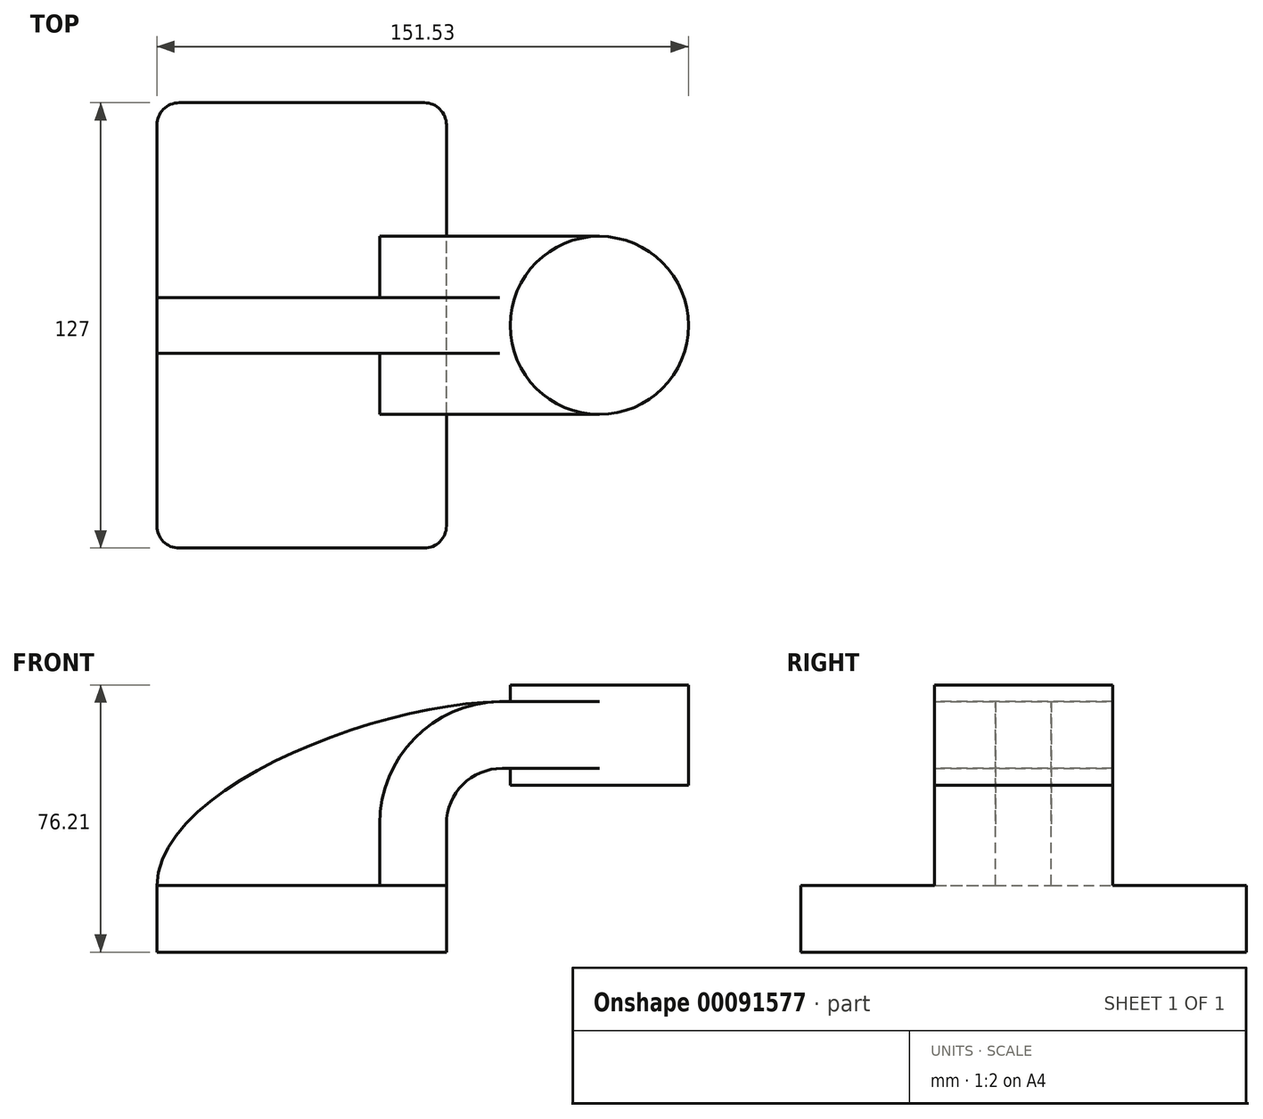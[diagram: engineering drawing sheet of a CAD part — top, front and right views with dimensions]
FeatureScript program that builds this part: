
annotation { "Feature Type Name" : "Feature", "Feature Type Description" : "" }
export const myFeature = defineFeature(function(context is Context, id is Id, definition is map)
    precondition{}
    {
        {
            var Q0;
            Q0=qCreatedBy(makeId("Front.planeOp"),FACE);
            var sketch = newSketch(context, id + "F0", { "sketchPlane" : qUnion([Q0])});
            skLineSegment(sketch, "E0.bottom", {"start": v(41.27, 9.53) * mm, "end": v(-41.28, 9.53) * mm});
            skLineSegment(sketch, "E0.top", {"start": v(41.28, -9.52) * mm, "end": v(-41.27, -9.52) * mm});
            skLineSegment(sketch, "E0.left", {"start": v(41.28, 9.53) * mm, "end": v(41.28, -9.52) * mm});
            skLineSegment(sketch, "E0.right", {"start": v(-41.28, 9.53) * mm, "end": v(-41.27, -9.52) * mm});
            skPoint(sketch, "E0.middle", {"position": v(0, 0) * mm});
            skLineSegment(sketch, "E1.bottom", {"start": v(59.45, 66.68) * mm, "end": v(110.25, 66.68) * mm});
            skLineSegment(sketch, "E1.top", {"start": v(59.45, 38.1) * mm, "end": v(110.25, 38.1) * mm});
            skLineSegment(sketch, "E1.left", {"start": v(59.45, 66.68) * mm, "end": v(59.45, 38.1) * mm});
            skLineSegment(sketch, "E1.right", {"start": v(110.25, 66.68) * mm, "end": v(110.25, 38.1) * mm});
            skPoint(sketch, "E1.middle", {"position": v(84.85, 52.39) * mm});
            skLineSegment(sketch, "E2", {"start": v(41.27, 9.53) * mm, "end": v(41.27, 27) * mm});
            skArc(sketch, "E3", {"start": v(41.27, 27) * mm, "mid": v(45.92, 38.23) * mm, "end": v(57.15, 42.88) * mm});
            skLineSegment(sketch, "E4", {"start": v(57.15, 42.88) * mm, "end": v(85.73, 42.88) * mm});
            skLineSegment(sketch, "E5.0", {"start": v(57.15, 61.93) * mm, "end": v(84.85, 61.93) * mm});
            skArc(sketch, "E5.1", {"start": v(22.22, 27) * mm, "mid": v(32.45, 51.7) * mm, "end": v(57.15, 61.93) * mm});
            skLineSegment(sketch, "E5.2", {"start": v(22.22, 9.53) * mm, "end": v(22.22, 27) * mm});
            skFitSpline(sketch, "E6", {"points": [v(-41.28, 9.53) * mm, v(57.15, 61.93) * mm], "startDerivative": vector(2.4, 85.45) * mm, "endDerivative": vector(103.27, 0.61) * mm});
            skLineSegment(sketch, "E7", {"start": v(84.85, 66.68) * mm, "end": v(84.85, 38.1) * mm});
            skSolve(sketch);
        }
        {
            var Q0;
            Q0=makeQuery(id+"F0.imprint","IMPRINT",FACE,{"disambiguationData":[TD([[makeQuery(id+"F0.imprint","IMPRINT",EDGE,{"derivedFrom":sQuery(id+"F0.wireOp",EDGE,"E0.top")}),-1.0]])]});
            extrude(context, id + "F1", {"entities" : qUnion([Q0]), "endBound" : BoundingType.SYMMETRIC, "depth" : 127 * mm});
        }
        {
            var Q0;
            {var subQ5=sQuery(id+"F0.wireOp",EDGE,"E2");Q0=makeQuery(id+"F0.imprint","IMPRINT",FACE,{"disambiguationData":[TD([[makeQuery(id+"F0.imprint","IMPRINT",EDGE,{"derivedFrom":subQ5}),1.0]])]});}
            var Q1;
            {var subQ0=sQuery(id+"F0.wireOp",EDGE,"E5.0");var subQ1=sQuery(id+"F0.wireOp",EDGE,"E1.left");var subQ2=makeQuery(id+"F0.imprint","INTERSECT",VERTEX,{"derivedFrom":[subQ1,subQ0]});Q1=makeQuery(id+"F0.imprint","IMPRINT",FACE,{"disambiguationData":[TD([[makeQuery(id+"F0.imprint","IMPRINT",EDGE,{"disambiguationData":[TD([[subQ2,-1.0]])],"derivedFrom":subQ1}),1.0]])]});}
            extrude(context, id + "F2", {"entities" : qUnion([Q0, Q1]), "operationType" : NewBodyOperationType.ADD, "endBound" : BoundingType.SYMMETRIC, "depth" : 50.8 * mm});
        }
        {
            var Q0;
            {var subQ3=sQuery(id+"F0.wireOp",EDGE,"E5.2");Q0=makeQuery(id+"F0.imprint","IMPRINT",FACE,{"disambiguationData":[TD([[makeQuery(id+"F0.imprint","IMPRINT",EDGE,{"derivedFrom":subQ3}),1.0]])]});}
            extrude(context, id + "F3", {"entities" : qUnion([Q0]), "operationType" : NewBodyOperationType.ADD, "endBound" : BoundingType.SYMMETRIC, "depth" : 15.88 * mm});
        }
        {
            var Q0;
            {var subQ0=sQuery(id+"F0.wireOp",EDGE,"E1.right");Q0=makeQuery(id+"F0.imprint","IMPRINT",FACE,{"disambiguationData":[TD([[makeQuery(id+"F0.imprint","IMPRINT",EDGE,{"derivedFrom":subQ0}),-1.0]])]});}
            var Q1;
            Q1=sQuery(id+"F0.wireOp",EDGE,"E7");
            revolve(context, id + "F4", {"operationType" : NewBodyOperationType.ADD, "entities" : qUnion([Q0]), "axis" : qUnion([Q1]), "revolveType" : RevolveType.FULL});
        }
        {
            var Q0;
            Q0=makeQuery(id+"F1.opExtrude","CAP_EDGE",EDGE,{"disambiguationData":[OSD([sQuery(id+"F0.wireOp",EDGE,"E0.right")])],"isStart":false});
            var Q1;
            Q1=makeQuery(id+"F1.opExtrude","CAP_EDGE",EDGE,{"disambiguationData":[OSD([sQuery(id+"F0.wireOp",EDGE,"E0.left")])],"isStart":false});
            var Q2;
            Q2=makeQuery(id+"F1.opExtrude","CAP_EDGE",EDGE,{"disambiguationData":[OSD([sQuery(id+"F0.wireOp",EDGE,"E0.left")])],"isStart":true});
            var Q3;
            Q3=makeQuery(id+"F1.opExtrude","CAP_EDGE",EDGE,{"disambiguationData":[OSD([sQuery(id+"F0.wireOp",EDGE,"E0.right")])],"isStart":true});
            fillet(context, id + "F5", {"entities" : qUnion([Q0, Q1, Q2, Q3]), "radius" : 6.35 * mm, "tangentPropagation" : true, "allowEdgeOverflow" : false});
        }
    });
